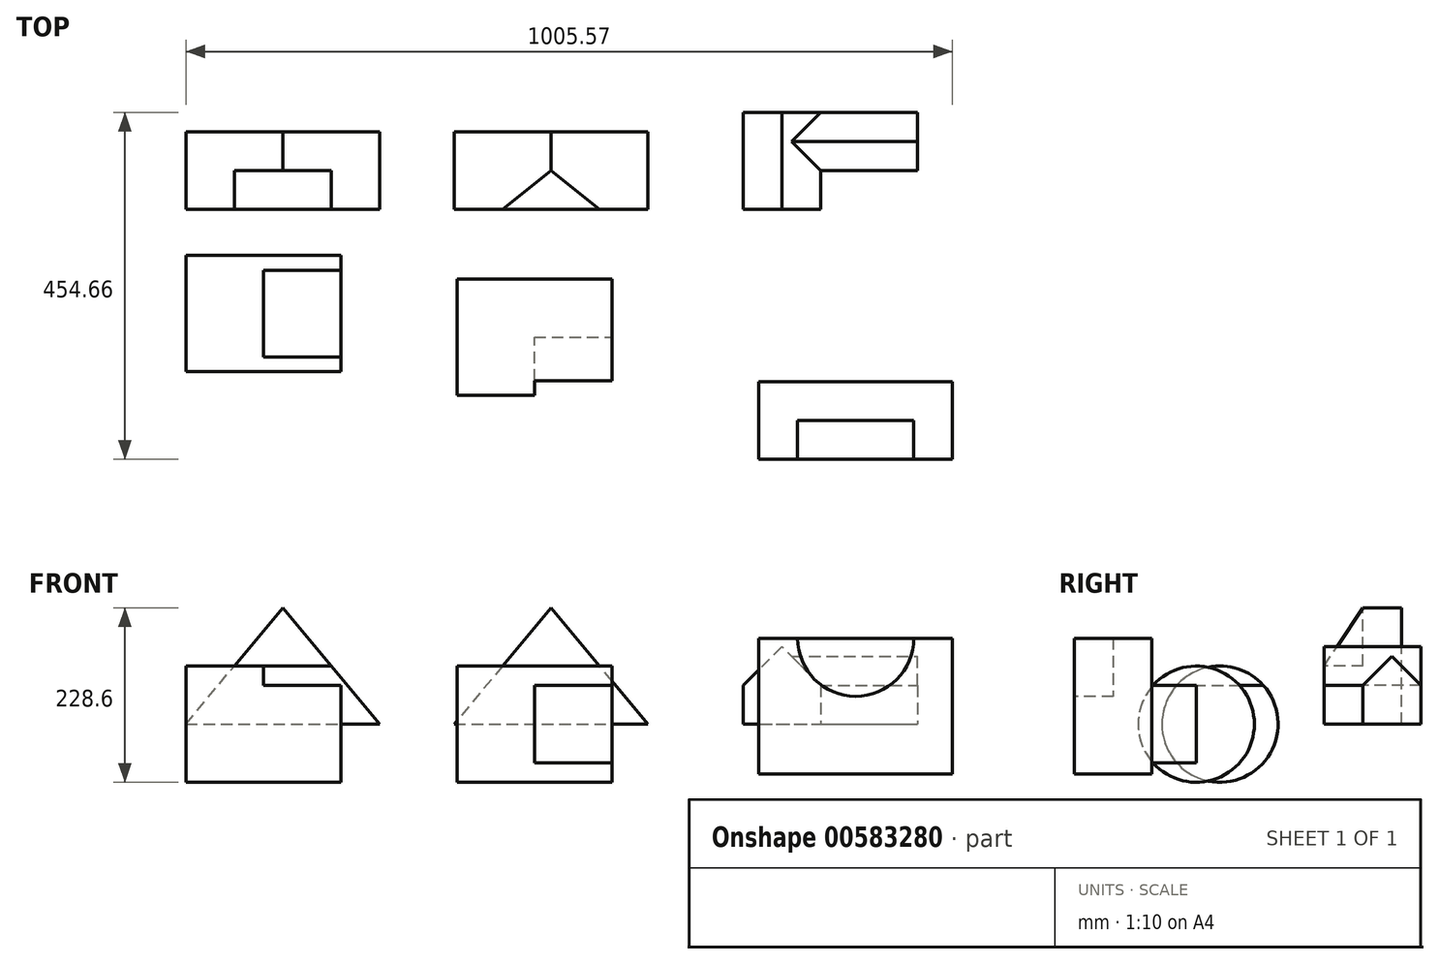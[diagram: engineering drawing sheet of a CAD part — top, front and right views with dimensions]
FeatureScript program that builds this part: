
annotation { "Feature Type Name" : "Feature", "Feature Type Description" : "" }
export const myFeature = defineFeature(function(context is Context, id is Id, definition is map)
    precondition{}
    {
        {
            var Q0;
            Q0=qCreatedBy(makeId("Front.planeOp"),FACE);
            var sketch = newSketch(context, id + "F0", { "sketchPlane" : qUnion([Q0])});
            skLineSegment(sketch, "E0", {"start": v(0, 0) * mm, "end": v(254, 0) * mm});
            skLineSegment(sketch, "E1", {"start": v(0, 0) * mm, "end": v(127, 152.4) * mm});
            skLineSegment(sketch, "E2", {"start": v(127, 152.4) * mm, "end": v(254, 0) * mm});
            skSolve(sketch);
        }
        {
            var Q0;
            Q0=makeQuery(id+"F0.imprint","IMPRINT",FACE,{"disambiguationData":[TD([[makeQuery(id+"F0.imprint","IMPRINT",EDGE,{"derivedFrom":sQuery(id+"F0.wireOp",EDGE,"E0")}),1.0]])]});
            extrude(context, id + "F1", {"entities" : qUnion([Q0]), "oppositeDirection" : true, "depth" : 101.6 * mm, "offsetDistance" : 25.4 * mm});
        }
        {
            var Q0;
            Q0=makeQuery(id+"F1.opExtrude","CAP_FACE",FACE,{"disambiguationData":[OSD([sQuery(id+"F0.wireOp",EDGE,"E0"),sQuery(id+"F0.wireOp",EDGE,"E1"),sQuery(id+"F0.wireOp",EDGE,"E2")])],"isStart":true});
            var sketch = newSketch(context, id + "F2", { "sketchPlane" : qUnion([Q0])});
            skLineSegment(sketch, "E3", {"start": v(63.5, 76.2) * mm, "end": v(190.5, 76.2) * mm});
            skLineSegment(sketch, "E4", {"start": v(63.5, 76.2) * mm, "end": v(127, 152.4) * mm});
            skLineSegment(sketch, "E5", {"start": v(127, 152.4) * mm, "end": v(190.5, 76.2) * mm});
            skSolve(sketch);
        }
        {
            var Q0;
            Q0=makeQuery(id+"F2.imprint","IMPRINT",FACE,{"disambiguationData":[TD([[makeQuery(id+"F2.imprint","IMPRINT",EDGE,{"derivedFrom":sQuery(id+"F2.wireOp",EDGE,"E3")}),1.0]])]});
            extrude(context, id + "F3", {"entities" : qUnion([Q0]), "operationType" : NewBodyOperationType.REMOVE, "oppositeDirection" : true, "depth" : 50.8 * mm, "offsetDistance" : 25.4 * mm});
        }
        {
            var Q0;
            Q0=qCreatedBy(makeId("Front.planeOp"),FACE);
            var sketch = newSketch(context, id + "F4", { "sketchPlane" : qUnion([Q0])});
            skLineSegment(sketch, "E6", {"start": v(351.86, 0) * mm, "end": v(605.86, 0) * mm});
            skLineSegment(sketch, "E7", {"start": v(605.86, 0) * mm, "end": v(478.86, 152.4) * mm});
            skLineSegment(sketch, "E8", {"start": v(478.86, 152.4) * mm, "end": v(351.86, 0) * mm});
            skSolve(sketch);
        }
        {
            var Q0;
            Q0=makeQuery(id+"F4.imprint","IMPRINT",FACE,{"disambiguationData":[TD([[makeQuery(id+"F4.imprint","IMPRINT",EDGE,{"derivedFrom":sQuery(id+"F4.wireOp",EDGE,"E6")}),1.0]])]});
            extrude(context, id + "F5", {"entities" : qUnion([Q0]), "oppositeDirection" : true, "depth" : 101.6 * mm, "offsetDistance" : 25.4 * mm});
        }
        {
            var Q0;
            Q0=makeQuery(id+"F5.opExtrude","CAP_EDGE",EDGE,{"disambiguationData":[OSD([sQuery(id+"F4.wireOp",EDGE,"E6")])],"isStart":true});
            cPoint(context, id + "F6", {"entities" : qUnion([Q0]), "parameter" : 0.5});
        }
        {
            var Q0;
            Q0=makeQuery(id+"F5.opExtrude","CAP_VERTEX",VERTEX,{"disambiguationData":[OSD([sQuery(id+"F4.wireOp",EDGE,"E7"),sQuery(id+"F4.wireOp",EDGE,"E8")])],"isStart":true});
            var Q1;
            Q1=makeQuery(id+"F5.opExtrude","CAP_VERTEX",VERTEX,{"disambiguationData":[OSD([sQuery(id+"F4.wireOp",EDGE,"E7"),sQuery(id+"F4.wireOp",EDGE,"E8")])],"isStart":false});
            var Q2;
            Q2 = qCreatedBy(id + "F6" ,VERTEX);
            cPlane(context, id + "F7", {"entities" : qUnion([Q0, Q1, Q2]), "cplaneType" : CPlaneType.THREE_POINT, "offset" : 25.4 * mm, "width" : 152.4 * mm, "height" : 152.4 * mm});
        }
        {
            var Q0;
            Q0=qCreatedBy(id+"F7.planeOp",FACE);
            var sketch = newSketch(context, id + "F8", { "sketchPlane" : qUnion([Q0])});
            skLineSegment(sketch, "E9", {"start": v(0, 76.2) * mm, "end": v(50.8, 152.4) * mm});
            skLineSegment(sketch, "E10", {"start": v(50.8, 152.4) * mm, "end": v(0, 152.4) * mm});
            skLineSegment(sketch, "E11", {"start": v(0, 152.4) * mm, "end": v(0, 76.2) * mm});
            skSolve(sketch);
        }
        {
            var Q0;
            Q0 = qSketchRegion(id + "F8", true);
            extrude(context, id + "F9", {"entities" : qUnion([Q0]), "operationType" : NewBodyOperationType.REMOVE, "endBound" : BoundingType.SYMMETRIC, "oppositeDirection" : true, "depth" : 152.4 * mm, "offsetDistance" : 25.4 * mm});
        }
        {
            var Q0;
            Q0=qCreatedBy(makeId("Front.planeOp"),FACE);
            var sketch = newSketch(context, id + "F10", { "sketchPlane" : qUnion([Q0])});
            skLineSegment(sketch, "E12", {"start": v(730.98, 0) * mm, "end": v(832.58, 0) * mm});
            skLineSegment(sketch, "E13", {"start": v(832.58, 0) * mm, "end": v(832.58, 50.8) * mm});
            skLineSegment(sketch, "E14", {"start": v(832.58, 50.8) * mm, "end": v(781.78, 101.6) * mm});
            skLineSegment(sketch, "E15", {"start": v(781.78, 101.6) * mm, "end": v(730.98, 50.8) * mm});
            skLineSegment(sketch, "E16", {"start": v(730.98, 50.8) * mm, "end": v(730.98, 0) * mm});
            skSolve(sketch);
        }
        {
            var Q0;
            Q0=makeQuery(id+"F10.imprint","IMPRINT",FACE,{"disambiguationData":[TD([[makeQuery(id+"F10.imprint","IMPRINT",EDGE,{"derivedFrom":sQuery(id+"F10.wireOp",EDGE,"E12")}),1.0]])]});
            extrude(context, id + "F11", {"entities" : qUnion([Q0]), "oppositeDirection" : true, "depth" : 127 * mm, "offsetDistance" : 25.4 * mm});
        }
        {
            var Q0;
            Q0=makeQuery(id+"F11.opExtrude","SWEPT_FACE",FACE,{"disambiguationData":[OSD([sQuery(id+"F10.wireOp",EDGE,"E13")])]});
            cPlane(context, id + "F12", {"entities" : qUnion([Q0]), "cplaneType" : CPlaneType.OFFSET, "offset" : 127 * mm, "width" : 152.4 * mm, "height" : 152.4 * mm});
        }
        {
            var Q0;
            Q0=qCreatedBy(id+"F12.planeOp",FACE);
            var sketch = newSketch(context, id + "F13", { "sketchPlane" : qUnion([Q0])});
            skLineSegment(sketch, "E17", {"start": v(50.8, 0) * mm, "end": v(50.8, 50.8) * mm});
            skLineSegment(sketch, "E18", {"start": v(50.8, 50.8) * mm, "end": v(88.9, 88.9) * mm});
            skLineSegment(sketch, "E19", {"start": v(88.9, 88.9) * mm, "end": v(127, 50.8) * mm});
            skLineSegment(sketch, "E20", {"start": v(127, 50.8) * mm, "end": v(127, 0) * mm});
            skLineSegment(sketch, "E21", {"start": v(127, 0) * mm, "end": v(50.8, 0) * mm});
            skSolve(sketch);
        }
        {
            var Q0;
            Q0=makeQuery(id+"F13.imprint","IMPRINT",FACE,{"disambiguationData":[TD([[makeQuery(id+"F13.imprint","IMPRINT",EDGE,{"derivedFrom":sQuery(id+"F13.wireOp",EDGE,"E17")}),-1.0]])]});
            extrude(context, id + "F14", {"entities" : qUnion([Q0]), "operationType" : NewBodyOperationType.ADD, "endBound" : BoundingType.UP_TO_NEXT, "oppositeDirection" : true, "depth" : 149.86 * mm, "offsetDistance" : 25.4 * mm});
        }
        {
            var Q0;
            Q0=qCreatedBy(makeId("Right.planeOp"),FACE);
            var sketch = newSketch(context, id + "F15", { "sketchPlane" : qUnion([Q0])});
            skCircle(sketch, "E22", {"center": v(-136.72, 0) * mm, "radius": 76.2 * mm});
            skSolve(sketch);
        }
        {
            var Q0;
            Q0=makeQuery(id+"F15.imprint","IMPRINT",FACE,{"disambiguationData":[TD([[makeQuery(id+"F15.imprint","IMPRINT",EDGE,{"derivedFrom":sQuery(id+"F15.wireOp",EDGE,"E22")}),1.0]])]});
            extrude(context, id + "F16", {"entities" : qUnion([Q0]), "depth" : 203.2 * mm, "offsetDistance" : 25.4 * mm});
        }
        {
            var Q0;
            Q0=makeQuery(id+"F16.opExtrude","CAP_FACE",FACE,{"disambiguationData":[OSD([sQuery(id+"F15.wireOp",EDGE,"E22")])],"isStart":false});
            var sketch = newSketch(context, id + "F17", { "sketchPlane" : qUnion([Q0])});
            skLineSegment(sketch, "E23", {"start": v(-193.52, 50.8) * mm, "end": v(-79.93, 50.8) * mm});
            skSolve(sketch);
        }
        {
            var Q0;
            {var subQ0=sQuery(id+"F17.wireOp",EDGE,"E23");Q0=makeQuery(id+"F17.imprint","IMPRINT",FACE,{"disambiguationData":[TD([[makeQuery(id+"F17.imprint","IMPRINT",EDGE,{"derivedFrom":subQ0}),1.0]])]});}
            extrude(context, id + "F18", {"entities" : qUnion([Q0]), "operationType" : NewBodyOperationType.REMOVE, "oppositeDirection" : true, "depth" : 101.6 * mm, "offsetDistance" : 25.4 * mm});
        }
        {
            var Q0;
            Q0=qCreatedBy(makeId("Right.planeOp"),FACE);
            cPlane(context, id + "F19", {"entities" : qUnion([Q0]), "cplaneType" : CPlaneType.OFFSET, "offset" : 355.6 * mm, "width" : 152.4 * mm, "height" : 152.4 * mm});
        }
        {
            var Q0;
            Q0=qCreatedBy(id+"F19.planeOp",FACE);
            var sketch = newSketch(context, id + "F20", { "sketchPlane" : qUnion([Q0])});
            skCircle(sketch, "E24", {"center": v(-167.85, 0) * mm, "radius": 76.2 * mm});
            skSolve(sketch);
        }
        {
            var Q0;
            Q0=makeQuery(id+"F20.imprint","IMPRINT",FACE,{"disambiguationData":[TD([[makeQuery(id+"F20.imprint","IMPRINT",EDGE,{"derivedFrom":sQuery(id+"F20.wireOp",EDGE,"E24")}),1.0]])]});
            extrude(context, id + "F21", {"entities" : qUnion([Q0]), "depth" : 203.2 * mm, "offsetDistance" : 25.4 * mm});
        }
        {
            var Q0;
            Q0=qCreatedBy(makeId("Front.planeOp"),FACE);
            cPlane(context, id + "F22", {"entities" : qUnion([Q0]), "cplaneType" : CPlaneType.OFFSET, "offset" : 226.06 * mm, "width" : 152.4 * mm, "height" : 152.4 * mm});
        }
        {
            var Q0;
            Q0=makeQuery(id+"F21.opExtrude","CAP_FACE",FACE,{"disambiguationData":[OSD([sQuery(id+"F20.wireOp",EDGE,"E24")])],"isStart":false});
            var sketch = newSketch(context, id + "F23", { "sketchPlane" : qUnion([Q0])});
            skLineSegment(sketch, "E25", {"start": v(-224.65, 50.8) * mm, "end": v(-167.85, 50.8) * mm});
            skLineSegment(sketch, "E26", {"start": v(-167.85, 50.8) * mm, "end": v(-167.85, -50.8) * mm});
            skLineSegment(sketch, "E27", {"start": v(-167.85, -50.8) * mm, "end": v(-224.65, -50.8) * mm});
            skSolve(sketch);
        }
        {
            var Q0;
            {var subQ0=sQuery(id+"F23.wireOp",EDGE,"E25");Q0=makeQuery(id+"F23.imprint","IMPRINT",FACE,{"disambiguationData":[TD([[makeQuery(id+"F23.imprint","IMPRINT",EDGE,{"derivedFrom":subQ0}),-1.0]])]});}
            extrude(context, id + "F24", {"entities" : qUnion([Q0]), "operationType" : NewBodyOperationType.REMOVE, "oppositeDirection" : true, "depth" : 101.6 * mm, "offsetDistance" : 25.4 * mm});
        }
        {
            var Q0;
            Q0=qCreatedBy(id+"F22.planeOp",FACE);
            var sketch = newSketch(context, id + "F25", { "sketchPlane" : qUnion([Q0])});
            skLineSegment(sketch, "E28", {"start": v(751.57, -65.18) * mm, "end": v(1005.57, -65.18) * mm});
            skLineSegment(sketch, "E29", {"start": v(1005.57, -65.18) * mm, "end": v(1005.57, 112.62) * mm});
            skLineSegment(sketch, "E30", {"start": v(1005.57, 112.62) * mm, "end": v(751.57, 112.62) * mm});
            skLineSegment(sketch, "E31", {"start": v(751.57, 112.62) * mm, "end": v(751.57, -65.18) * mm});
            skSolve(sketch);
        }
        {
            var Q0;
            Q0 = qSketchRegion(id + "F25", true);
            extrude(context, id + "F26", {"entities" : qUnion([Q0]), "operationType" : NewBodyOperationType.ADD, "depth" : 101.6 * mm, "offsetDistance" : 25.4 * mm});
        }
        {
            var Q0;
            Q0=makeQuery(id+"F26.opExtrude","CAP_FACE",FACE,{"disambiguationData":[OSD([sQuery(id+"F25.wireOp",EDGE,"E28"),sQuery(id+"F25.wireOp",EDGE,"E29"),sQuery(id+"F25.wireOp",EDGE,"E30"),sQuery(id+"F25.wireOp",EDGE,"E31")])],"isStart":false});
            var sketch = newSketch(context, id + "F27", { "sketchPlane" : qUnion([Q0])});
            skCircle(sketch, "E32", {"center": v(878.57, 112.62) * mm, "radius": 76.2 * mm});
            skSolve(sketch);
        }
        {
            var Q0;
            {var subQ0=sQuery(id+"F27.wireOp",EDGE,"E32");var subQ1=makeQuery(id+"F26.opExtrude","CAP_EDGE",EDGE,{"disambiguationData":[OSD([sQuery(id+"F25.wireOp",EDGE,"E30")])],"isStart":false});var subQ2=makeQuery(id+"F27.imprint","INTERSECT",VERTEX,{"disambiguationData":[OD(0.0)],"derivedFrom":[subQ1,subQ0]});Q0=makeQuery(id+"F27.imprint","IMPRINT",FACE,{"disambiguationData":[TD([[makeQuery(id+"F27.imprint","IMPRINT",EDGE,{"disambiguationData":[TD([[subQ2,-1.0]])],"derivedFrom":subQ0}),1.0]])]});}
            var Q1;
            {var subQ0=sQuery(id+"F27.wireOp",EDGE,"E32");var subQ1=makeQuery(id+"F26.opExtrude","CAP_EDGE",EDGE,{"disambiguationData":[OSD([sQuery(id+"F25.wireOp",EDGE,"E30")])],"isStart":false});var subQ2=makeQuery(id+"F27.imprint","INTERSECT",VERTEX,{"disambiguationData":[OD(0.0)],"derivedFrom":[subQ1,subQ0]});Q1=makeQuery(id+"F27.imprint","IMPRINT",FACE,{"disambiguationData":[TD([[makeQuery(id+"F27.imprint","IMPRINT",EDGE,{"disambiguationData":[TD([[subQ2,1.0]])],"derivedFrom":subQ0}),1.0]])]});}
            extrude(context, id + "F28", {"entities" : qUnion([Q0, Q1]), "operationType" : NewBodyOperationType.REMOVE, "oppositeDirection" : true, "depth" : 50.8 * mm, "offsetDistance" : 25.4 * mm});
        }
    });
